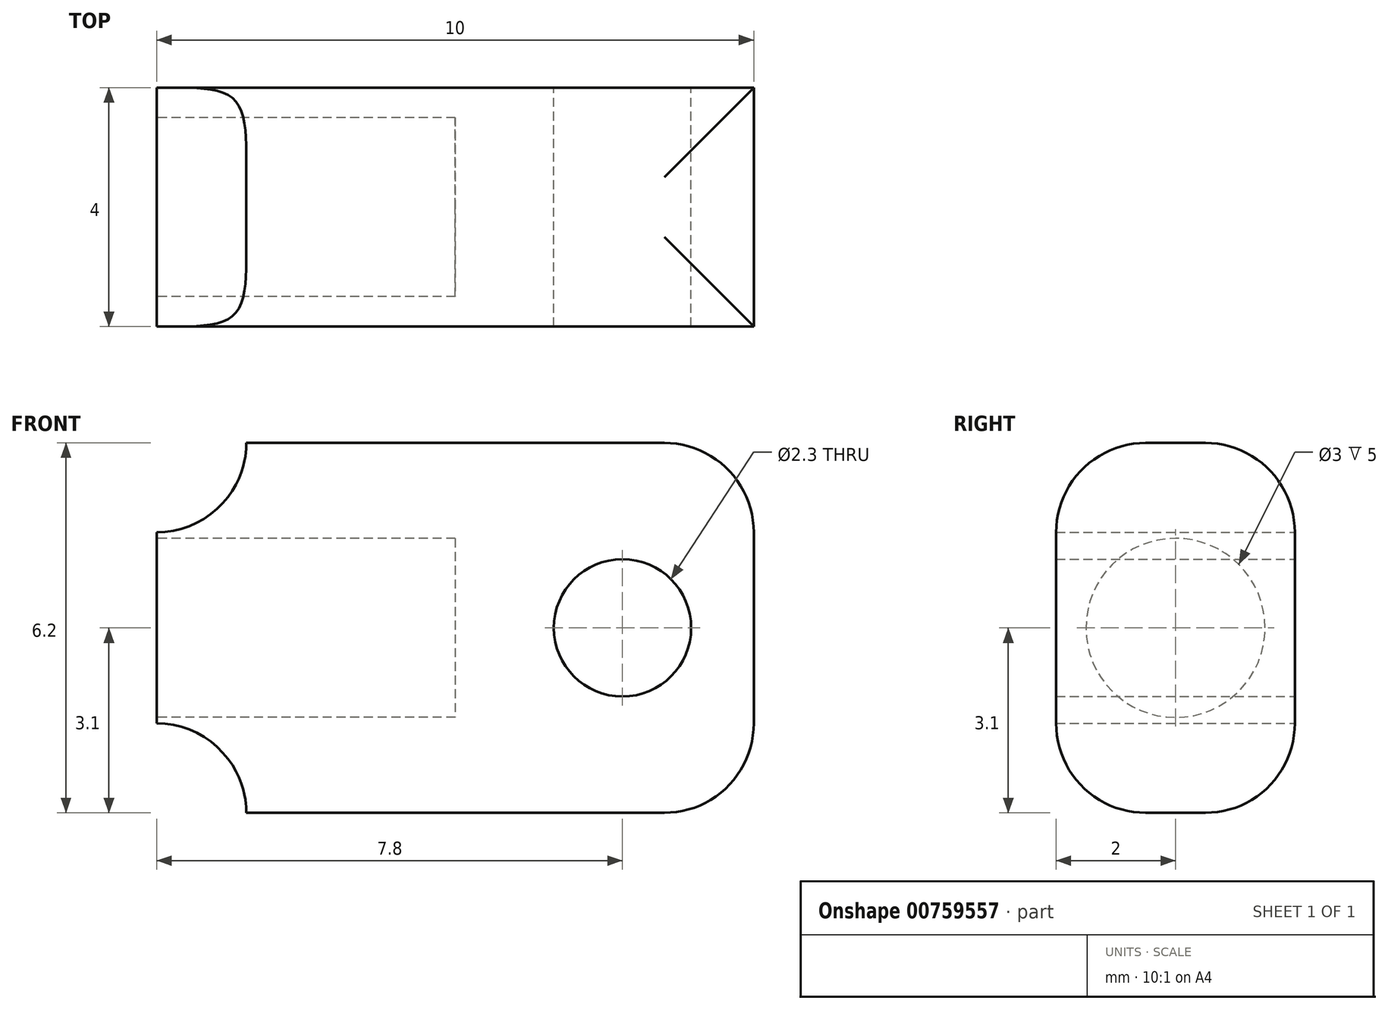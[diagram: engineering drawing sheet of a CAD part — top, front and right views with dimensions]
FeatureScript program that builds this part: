
annotation { "Feature Type Name" : "Feature", "Feature Type Description" : "" }
export const myFeature = defineFeature(function(context is Context, id is Id, definition is map)
    precondition{}
    {
        {
            var Q0;
            Q0=qCreatedBy(makeId("Front.planeOp"),FACE);
            var sketch = newSketch(context, id + "F0", { "sketchPlane" : qUnion([Q0])});
            skLineSegment(sketch, "E0.bottom", {"start": v(5, 3.1) * mm, "end": v(-3.5, 3.1) * mm});
            skLineSegment(sketch, "E0.top", {"start": v(5, -3.1) * mm, "end": v(-3.5, -3.1) * mm});
            skLineSegment(sketch, "E0.left", {"start": v(5, 3.1) * mm, "end": v(5, -3.1) * mm});
            skLineSegment(sketch, "E0.right", {"start": v(-5, 1.6) * mm, "end": v(-5, -1.6) * mm});
            skPoint(sketch, "E0.middle", {"position": v(0, 0) * mm});
            skArc(sketch, "E1", {"start": v(-5, 1.6) * mm, "mid": v(-3.94, 2.04) * mm, "end": v(-3.5, 3.1) * mm});
            skArc(sketch, "E2", {"start": v(-3.5, -3.1) * mm, "mid": v(-3.94, -2.04) * mm, "end": v(-5, -1.6) * mm});
            skCircle(sketch, "E3", {"center": v(2.8, 0) * mm, "radius": 1.15 * mm});
            skSolve(sketch);
        }
        {
            var Q0;
            Q0 = qSketchRegion(id + "F0", true);
            extrude(context, id + "F1", {"entities" : qUnion([Q0]), "depth" : 4 * mm, "offsetDistance" : 25 * mm});
        }
        {
            var Q0;
            Q0=makeQuery(id+"F1.opExtrude","SWEPT_FACE",FACE,{"disambiguationData":[OSD([sQuery(id+"F0.wireOp",EDGE,"E0.right")])]});
            var sketch = newSketch(context, id + "F2", { "sketchPlane" : qUnion([Q0])});
            skCircle(sketch, "E4", {"center": v(2, 0) * mm, "radius": 1.5 * mm});
            skSolve(sketch);
        }
        {
            var Q0;
            Q0 = qSketchRegion(id + "F2", true);
            extrude(context, id + "F3", {"entities" : qUnion([Q0]), "operationType" : NewBodyOperationType.REMOVE, "oppositeDirection" : true, "depth" : 5 * mm, "offsetDistance" : 25 * mm});
        }
        {
            var Q0;
            Q0=makeQuery(id+"F1.opExtrude","SWEPT_EDGE",EDGE,{"disambiguationData":[OSD([sQuery(id+"F0.wireOp",EDGE,"E0.bottom"),sQuery(id+"F0.wireOp",EDGE,"E0.left")])]});
            var Q1;
            Q1=makeQuery(id+"F1.opExtrude","SWEPT_EDGE",EDGE,{"disambiguationData":[OSD([sQuery(id+"F0.wireOp",EDGE,"E0.top"),sQuery(id+"F0.wireOp",EDGE,"E0.left")])]});
            var Q2;
            Q2=makeQuery(id+"F1.opExtrude","CAP_EDGE",EDGE,{"disambiguationData":[OSD([sQuery(id+"F0.wireOp",EDGE,"E0.bottom")])],"isStart":true});
            var Q3;
            Q3=makeQuery(id+"F1.opExtrude","CAP_EDGE",EDGE,{"disambiguationData":[OSD([sQuery(id+"F0.wireOp",EDGE,"E0.bottom")])],"isStart":false});
            var Q4;
            Q4=makeQuery(id+"F1.opExtrude","CAP_EDGE",EDGE,{"disambiguationData":[OSD([sQuery(id+"F0.wireOp",EDGE,"E0.top")])],"isStart":false});
            var Q5;
            Q5=makeQuery(id+"F1.opExtrude","CAP_EDGE",EDGE,{"disambiguationData":[OSD([sQuery(id+"F0.wireOp",EDGE,"E0.top")])],"isStart":true});
            fillet(context, id + "F4", {"entities" : qUnion([Q0, Q1, Q2, Q3, Q4, Q5]), "radius" : 1.5 * mm, "tangentPropagation" : true, "allowEdgeOverflow" : false});
        }
    });
